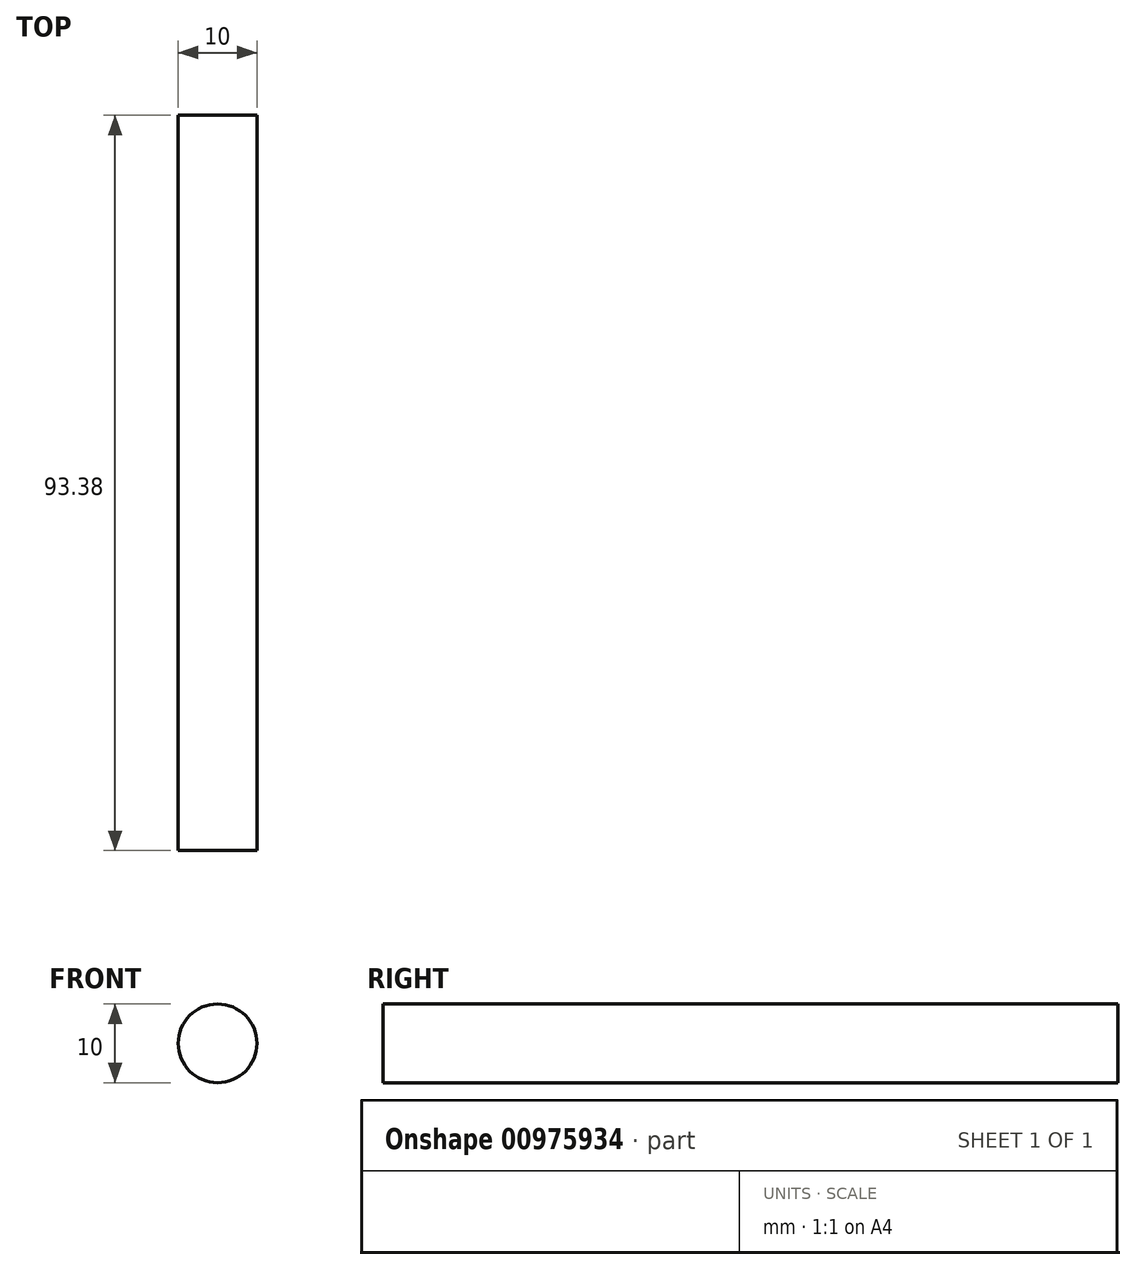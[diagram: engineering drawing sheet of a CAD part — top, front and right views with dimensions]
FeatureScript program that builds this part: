
annotation { "Feature Type Name" : "Feature", "Feature Type Description" : "" }
export const myFeature = defineFeature(function(context is Context, id is Id, definition is map)
    precondition{}
    {
        {
            var Q0;
            Q0=qCreatedBy(makeId("Front.planeOp"),FACE);
            var sketch = newSketch(context, id + "F0", { "sketchPlane" : qUnion([Q0])});
            skCircle(sketch, "E0", {"center": v(0, 0) * mm, "radius": 5 * mm});
            skSolve(sketch);
        }
        {
            var Q0;
            Q0=qCreatedBy(makeId("Right.planeOp"),FACE);
            var sketch = newSketch(context, id + "F1", { "sketchPlane" : qUnion([Q0])});
            skFitSpline(sketch, "E1", {"points": [v(0, 0) * mm, v(-43.36, 0) * mm, v(-90.38, 0) * mm], "startDerivative": vector(-64.3, 0) * mm, "endDerivative": vector(-52.85, 0) * mm});
            skSolve(sketch);
        }
        {
            var Q0;
            Q0=makeQuery(id+"F0.imprint","IMPRINT",FACE,{"disambiguationData":[TD([[makeQuery(id+"F0.imprint","IMPRINT",EDGE,{"derivedFrom":sQuery(id+"F0.wireOp",EDGE,"E0")}),1.0]])]});
            var Q1;
            Q1=sQuery(id+"F1.wireOp",EDGE,"E1");
            sweep(context, id + "F2", {"profiles" : qUnion([Q0]), "path" : qUnion([Q1])});
        }
        {
            var Q0;
            Q0=makeQuery(id+"F2.opSweep","CAP_FACE",FACE,{"disambiguationData":[OSD([sQuery(id+"F0.wireOp",EDGE,"E0"),sQuery(id+"F1.wireOp",VERTEX,"E1.end")])],"isStart":false});
            extrude(context, id + "F3", {"entities" : qUnion([Q0]), "operationType" : NewBodyOperationType.ADD, "depth" : 73 * mm, "offsetDistance" : 25 * mm});
        }
        {
            var Q0;
            Q0=makeQuery(id+"F3.opExtrude","CAP_FACE",FACE,{"disambiguationData":[OSD([sQuery(id+"F0.wireOp",EDGE,"E0"),sQuery(id+"F1.wireOp",VERTEX,"E1.end")])],"isStart":false});
            extrude(context, id + "F4", {"entities" : qUnion([Q0]), "operationType" : NewBodyOperationType.REMOVE, "oppositeDirection" : true, "depth" : 70 * mm, "offsetDistance" : 25 * mm});
        }
    });
